# Revit family: Mirror-IlluminatedMirrorCabinet-65cm-Vitra-ValarteSeries-62225+62226+62227+62228+62229+62230
name_source: partatom
category: Furniture Systems
revit_build: Autodesk Revit 2017 (Build: 20160225_1515(x64)
units: mm (PartAtom-declared; Revit-internal decimal feet)

## family parameters
Cut with Voids When Loaded = No
Host = Face
OmniClass Number = 23.40.00.00
OmniClass Title = Equipment and Furnishings
Part Type = Normal
Room Calculation Point = No
Round Connector Dimension = Use Diameter
Shared = Yes

## types (6) — shared parameters
BIMobject category = Storage
Construction Type = Wall Mounted
Default Elevation = 660 mm
Depth(mm) = 170 mm  [stored 0.557743 ft]
Description = Valarte Illuminated Cabinet Mirror
Design country = Turkey
Height(mm) = 760 mm
IFC Classification = Furnishing Element
Lighting Type = Ambiance Led Lighting
Manufacturer = Vitra
Manufacturer name = Vitra
Masterformat 2014 Code = 41 53 13
Masterformat 2014 Description = Storage Cabinets
NBS Referans Code = 35-75-08
NBS Referans Description = Bathroom Cabinets
Nominal height = 0.000
Nominal width = 0.000
OmniClass Code = 23-25 53 11 13 11
OmniClass Description = Medicine Cabinets
Product certification = https://vitraglobal.com
Product data url = https://www.vitra.co.uk
Product family = Valarte
Product group = Bathroom Furniture
Secondary Material = Vitra-Mirror
Technical description = https://www.vitra.co.uk
UNSPSC Code = 30161801
UNSPSC Description = Bathroom cabinets
URL = https://vitraglobal.com
Uniclass 1.4 Code = L72141
Uniclass 1.4 Description = Cabinets
Uniclass 2.0 Code = PR-35-75-08
Uniclass 2.0 Description = Bathroom Cabinets
Uniclass 2015 Code = Pr_40_30_78_03
Uniclass 2015 Name = Bathroom cabinets
Uniformat II Code = E20
Uniformat II Description = Furnishings
Voltage = 220V
Warranty Period (Year) = 2
Weight Net (kg) = 24,000
Width(mm) = 630 mm  [stored 2.06693 ft]
Youtube = https://www.youtube.com

## per-type parameters (varying)
| type | Article No. (default) | Model | Primary Material | Product SKU |
| MirrorCabinetLeft(Illuminated)-Vitra-ValarteSeries_62225 | 62225 | 62225 | Vitra-MattWhite | 62225 |
| MirrorCabinetLeft(Illuminated)-Vitra-ValarteSeries_62226 | 62226 | 62226 | Vitra-MattGrey | 62226 |
| MirrorCabinetLeft(Illuminated)-Vitra-ValarteSeries_62227 | 62227 | 62227 | Vitra-MattIvory | 62227 |
| MirrorCabinetRight(Illuminated)-Vitra-ValarteSeries_62228 | 62228 | 62228 | Vitra-MattWhite | 62228 |
| MirrorCabinetRight(Illuminated)-Vitra-ValarteSeries_62229 | 62229 | 62229 | Vitra-MattGrey | 62229 |
| MirrorCabinetRight(Illuminated)-Vitra-ValarteSeries_62230 | 62230 | 62230 | Vitra-MattIvory | 62230 |

note: [stored X ft] marks values corroborated as IEEE doubles in the binary element streams (Revit-internal decimal feet)

## geometry (parser evidence)
native form markers: Sweep x3
no freeform markers — native parametric forms only
